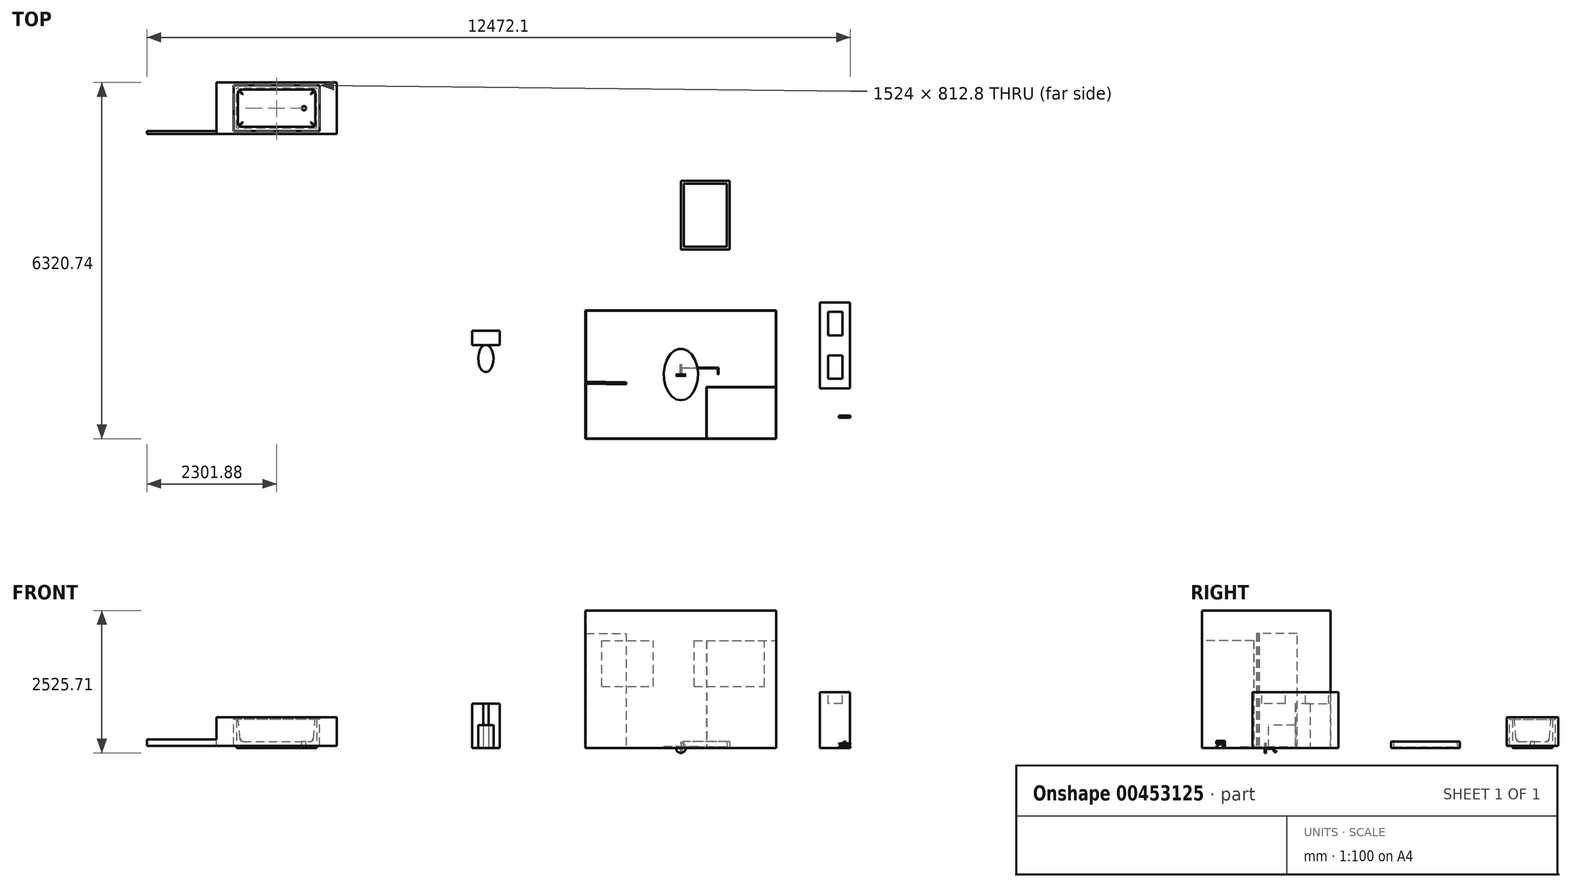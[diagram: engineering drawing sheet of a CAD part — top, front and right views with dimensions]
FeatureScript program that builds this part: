
annotation { "Feature Type Name" : "Feature", "Feature Type Description" : "" }
export const myFeature = defineFeature(function(context is Context, id is Id, definition is map)
    precondition{}
    {
        {
            var Q0;
            Q0=qCreatedBy(makeId("Top.planeOp"),FACE);
            var sketch = newSketch(context, id + "F0", { "sketchPlane" : qUnion([Q0])});
            skLineSegment(sketch, "E0.bottom", {"start": v(1684.34, 1131.89) * mm, "end": v(-1684.34, 1131.89) * mm});
            skLineSegment(sketch, "E0.top", {"start": v(1684.34, -1131.89) * mm, "end": v(-1684.34, -1131.89) * mm});
            skLineSegment(sketch, "E0.left", {"start": v(1684.34, 1131.89) * mm, "end": v(1684.34, -1131.89) * mm});
            skLineSegment(sketch, "E0.right", {"start": v(-1684.34, 1131.89) * mm, "end": v(-1684.34, -1131.89) * mm});
            skLineSegment(sketch, "E1.0", {"start": v(1690.69, 1138.24) * mm, "end": v(-1690.69, 1138.24) * mm});
            skLineSegment(sketch, "E1.1", {"start": v(1690.69, 1138.24) * mm, "end": v(1690.69, -1138.24) * mm});
            skLineSegment(sketch, "E1.2", {"start": v(1690.69, -1138.24) * mm, "end": v(-1690.69, -1138.24) * mm});
            skLineSegment(sketch, "E1.3", {"start": v(-1690.69, 1138.24) * mm, "end": v(-1690.69, -1138.24) * mm});
            skSolve(sketch);
        }
        {
            var Q0;
            Q0=makeQuery(id+"F0.imprint","IMPRINT",FACE,{"disambiguationData":[TD([[makeQuery(id+"F0.imprint","IMPRINT",EDGE,{"derivedFrom":sQuery(id+"F0.wireOp",EDGE,"E0.bottom")}),-1.0]])]});
            var Q1;
            {var subQ1=sQuery(id+"F0.wireOp",EDGE,"WMKTGaaz-quiy-9job-mGH0-Ok6Mli3DVS2J");Q1=makeQuery(id+"F0.imprint","IMPRINT",FACE,{"disambiguationData":[TD([[makeQuery(id+"F0.imprint","IMPRINT",EDGE,{"derivedFrom":subQ1}),-1.0]])]});}
            var Q2;
            Q2=sQuery(id+"F0.wireOp",EDGE,"E0.bottom");
            var Q3;
            Q3=sQuery(id+"F0.wireOp",EDGE,"E0.left");
            var Q4;
            Q4=sQuery(id+"F0.wireOp",EDGE,"E0.top");
            var Q5;
            Q5=sQuery(id+"F0.wireOp",EDGE,"E0.right");
            extrude(context, id + "F1", {"entities" : qUnion([Q0, Q1]), "surfaceEntities" : qUnion([Q2, Q3, Q4, Q5]), "depth" : 2438.4 * mm});
        }
        {
            var Q0;
            Q0=qCreatedBy(makeId("Top.planeOp"),FACE);
            var sketch = newSketch(context, id + "F2", { "sketchPlane" : qUnion([Q0])});
            skLineSegment(sketch, "E2.bottom", {"start": v(-6403.12, 4318.9) * mm, "end": v(-7927.12, 4318.9) * mm});
            skLineSegment(sketch, "E2.top", {"start": v(-6403.12, 5131.7) * mm, "end": v(-7927.12, 5131.7) * mm});
            skLineSegment(sketch, "E2.left", {"start": v(-6403.12, 4318.9) * mm, "end": v(-6403.12, 5131.7) * mm});
            skLineSegment(sketch, "E2.right", {"start": v(-7927.12, 4318.9) * mm, "end": v(-7927.12, 5131.7) * mm});
            skPoint(sketch, "E2.middle", {"position": v(-7165.12, 4725.3) * mm});
            skSolve(sketch);
        }
        {
            var Q0;
            Q0 = qSketchRegion(id + "F2", true);
            extrude(context, id + "F3", {"entities" : qUnion([Q0]), "depth" : 546.1 * mm});
        }
        {
            var Q0;
            Q0=makeQuery(id+"F3.opExtrude","CAP_FACE",FACE,{"disambiguationData":[OSD([sQuery(id+"F2.wireOp",EDGE,"E2.bottom"),sQuery(id+"F2.wireOp",EDGE,"E2.top"),sQuery(id+"F2.wireOp",EDGE,"E2.left"),sQuery(id+"F2.wireOp",EDGE,"E2.right")])],"isStart":false});
            var sketch = newSketch(context, id + "F4", { "sketchPlane" : qUnion([Q0])});
            skLineSegment(sketch, "E3.bottom", {"start": v(-6530.12, 5055.5) * mm, "end": v(-7800.12, 5055.5) * mm});
            skLineSegment(sketch, "E3.top", {"start": v(-6530.12, 4395.1) * mm, "end": v(-7800.12, 4395.1) * mm});
            skLineSegment(sketch, "E3.left", {"start": v(-6479.32, 5004.7) * mm, "end": v(-6479.32, 4445.9) * mm});
            skLineSegment(sketch, "E3.right", {"start": v(-7850.92, 5004.7) * mm, "end": v(-7850.92, 4445.9) * mm});
            skPoint(sketch, "E3.middle", {"position": v(-7165.12, 4725.3) * mm});
            skPoint(sketch, "E4.visualSharp", {"position": v(-7850.92, 5055.5) * mm});
            skArc(sketch, "E4.filletArc", {"start": v(-7800.12, 5055.5) * mm, "mid": v(-7836.05, 5040.62) * mm, "end": v(-7850.92, 5004.7) * mm});
            skPoint(sketch, "E5.visualSharp", {"position": v(-7850.92, 4395.1) * mm});
            skArc(sketch, "E5.filletArc", {"start": v(-7850.92, 4445.9) * mm, "mid": v(-7836.05, 4409.98) * mm, "end": v(-7800.12, 4395.1) * mm});
            skPoint(sketch, "E6.visualSharp", {"position": v(-6479.32, 4395.1) * mm});
            skArc(sketch, "E6.filletArc", {"start": v(-6530.12, 4395.1) * mm, "mid": v(-6494.2, 4409.98) * mm, "end": v(-6479.32, 4445.9) * mm});
            skPoint(sketch, "E7.visualSharp", {"position": v(-6479.32, 5055.5) * mm});
            skArc(sketch, "E7.filletArc", {"start": v(-6479.32, 5004.7) * mm, "mid": v(-6494.2, 5040.62) * mm, "end": v(-6530.12, 5055.5) * mm});
            skSolve(sketch);
        }
        {
            var Q0;
            Q0=makeQuery(id+"F4.imprint","IMPRINT",FACE,{"disambiguationData":[TD([[makeQuery(id+"F4.imprint","IMPRINT",EDGE,{"derivedFrom":sQuery(id+"F4.wireOp",EDGE,"E3.bottom")}),1.0]])]});
            extrude(context, id + "F5", {"entities" : qUnion([Q0]), "operationType" : NewBodyOperationType.REMOVE, "oppositeDirection" : true, "depth" : 431.8 * mm, "hasDraft" : true, "draftAngle" : 5 * degree, "draftPullDirection" : true});
        }
        {
            var Q0;
            Q0=makeQuery(id+"F3.opExtrude","CAP_FACE",FACE,{"disambiguationData":[OSD([sQuery(id+"F2.wireOp",EDGE,"E2.bottom"),sQuery(id+"F2.wireOp",EDGE,"E2.top"),sQuery(id+"F2.wireOp",EDGE,"E2.left"),sQuery(id+"F2.wireOp",EDGE,"E2.right")])],"isStart":false});
            var sketch = newSketch(context, id + "F6", { "sketchPlane" : qUnion([Q0])});
            skLineSegment(sketch, "E8.0.0", {"start": v(-6403.12, 4318.9) * mm, "end": v(-6403.12, 5131.7) * mm});
            skLineSegment(sketch, "E8.0.1", {"start": v(-6403.12, 5131.7) * mm, "end": v(-7927.12, 5131.7) * mm});
            skLineSegment(sketch, "E8.0.2", {"start": v(-7927.12, 5131.7) * mm, "end": v(-7927.12, 4318.9) * mm});
            skLineSegment(sketch, "E8.0.3", {"start": v(-7927.12, 4318.9) * mm, "end": v(-6403.12, 4318.9) * mm});
            skLineSegment(sketch, "E9.0", {"start": v(-6352.32, 5182.5) * mm, "end": v(-7977.92, 5182.5) * mm});
            skLineSegment(sketch, "E9.1", {"start": v(-6352.32, 4268.1) * mm, "end": v(-6352.32, 5182.5) * mm});
            skLineSegment(sketch, "E9.2", {"start": v(-7977.92, 4268.1) * mm, "end": v(-6352.32, 4268.1) * mm});
            skLineSegment(sketch, "E9.3", {"start": v(-7977.92, 5182.5) * mm, "end": v(-7977.92, 4268.1) * mm});
            skSolve(sketch);
        }
        {
            var Q0;
            Q0 = qSketchRegion(id + "F6", true);
            var Q1;
            Q1=makeQuery(id+"F3.opExtrude","CAP_FACE",FACE,{"disambiguationData":[OSD([sQuery(id+"F2.wireOp",EDGE,"E2.bottom"),sQuery(id+"F2.wireOp",EDGE,"E2.top"),sQuery(id+"F2.wireOp",EDGE,"E2.left"),sQuery(id+"F2.wireOp",EDGE,"E2.right")])],"isStart":true});
            extrude(context, id + "F7", {"entities" : qUnion([Q0]), "oppositeDirection" : true, "endBoundEntityFace" : qUnion([Q1]), "depth" : 508 * mm});
        }
        {
            var Q0;
            Q0=makeQuery(id+"F1.opExtrude","SWEPT_FACE",FACE,{"disambiguationData":[OSD([sQuery(id+"F0.wireOp",EDGE,"E0.bottom")])]});
            var sketch = newSketch(context, id + "F8", { "sketchPlane" : qUnion([Q0])});
            skLineSegment(sketch, "E10.bottom", {"start": v(-1404.94, 1092.2) * mm, "end": v(-490.54, 1092.2) * mm});
            skLineSegment(sketch, "E10.top", {"start": v(-1404.94, 1905) * mm, "end": v(-490.54, 1905) * mm});
            skLineSegment(sketch, "E10.left", {"start": v(-1404.94, 1092.2) * mm, "end": v(-1404.94, 1905) * mm});
            skLineSegment(sketch, "E10.right", {"start": v(-490.54, 1092.2) * mm, "end": v(-490.54, 1905) * mm});
            skLineSegment(sketch, "E11.bottom", {"start": v(233.36, 1092.2) * mm, "end": v(1481.14, 1092.2) * mm});
            skLineSegment(sketch, "E11.top", {"start": v(233.36, 1905) * mm, "end": v(1481.14, 1905) * mm});
            skLineSegment(sketch, "E11.left", {"start": v(233.36, 1092.2) * mm, "end": v(233.36, 1905) * mm});
            skLineSegment(sketch, "E11.right", {"start": v(1481.14, 1092.2) * mm, "end": v(1481.14, 1905) * mm});
            skSolve(sketch);
        }
        {
            var Q0;
            Q0 = qSketchRegion(id + "F8", true);
            extrude(context, id + "F9", {"entities" : qUnion([Q0]), "operationType" : NewBodyOperationType.REMOVE, "endBound" : BoundingType.THROUGH_ALL, "oppositeDirection" : true, "depth" : 25.4 * mm});
        }
        {
            var Q0;
            Q0=qCreatedBy(makeId("Top.planeOp"),FACE);
            var sketch = newSketch(context, id + "F10", { "sketchPlane" : qUnion([Q0])});
            skEllipse(sketch, "E12", {"center": v(-3457.47, 284.68) * mm, "majorRadius": 240.93 * mm, "minorRadius": 135.6 * mm, "majorAxis": v(0, 1)});
            skLineSegment(sketch, "E13.bottom", {"start": v(-3701.15, 777.17) * mm, "end": v(-3213.79, 777.17) * mm});
            skLineSegment(sketch, "E13.top", {"start": v(-3701.15, 525.6) * mm, "end": v(-3213.79, 525.6) * mm});
            skLineSegment(sketch, "E13.left", {"start": v(-3701.15, 777.17) * mm, "end": v(-3701.15, 525.6) * mm});
            skLineSegment(sketch, "E13.right", {"start": v(-3213.79, 777.17) * mm, "end": v(-3213.79, 525.6) * mm});
            skPoint(sketch, "E14", {"position": v(-3457.47, 43.75) * mm});
            skPoint(sketch, "E15", {"position": v(-3457.47, 525.6) * mm});
            skLineSegment(sketch, "E16.bottom", {"start": v(-3410.99, 490.28) * mm, "end": v(-3503.95, 490.28) * mm});
            skLineSegment(sketch, "E16.top", {"start": v(-3410.99, 560.94) * mm, "end": v(-3503.95, 560.94) * mm});
            skLineSegment(sketch, "E16.left", {"start": v(-3410.99, 490.28) * mm, "end": v(-3410.99, 560.94) * mm});
            skLineSegment(sketch, "E16.right", {"start": v(-3503.95, 490.28) * mm, "end": v(-3503.95, 560.94) * mm});
            skSolve(sketch);
        }
        {
            var Q0;
            Q0 = qSketchRegion(id + "F10", true);
            extrude(context, id + "F11", {"entities" : qUnion([Q0]), "depth" : 784.22 * mm});
        }
        {
            var Q0;
            Q0=makeQuery(id+"F11.opExtrude","CAP_FACE",FACE,{"disambiguationData":[OSD([sQuery(id+"F10.wireOp",EDGE,"E12"),sQuery(id+"F10.wireOp",EDGE,"E13.bottom"),sQuery(id+"F10.wireOp",EDGE,"E13.top"),sQuery(id+"F10.wireOp",EDGE,"E13.left"),sQuery(id+"F10.wireOp",EDGE,"E13.right"),sQuery(id+"F10.wireOp",EDGE,"E16.left"),sQuery(id+"F10.wireOp",EDGE,"E16.right")])],"isStart":false});
            var sketch = newSketch(context, id + "F12", { "sketchPlane" : qUnion([Q0])});
            skEllipse(sketch, "E17", {"center": v(-3457.47, 284.68) * mm, "majorRadius": 240.93 * mm, "minorRadius": 135.6 * mm, "majorAxis": v(0, -1)});
            skSolve(sketch);
        }
        {
            var Q0;
            Q0 = qSketchRegion(id + "F12", true);
            extrude(context, id + "F13", {"entities" : qUnion([Q0]), "operationType" : NewBodyOperationType.REMOVE, "oppositeDirection" : true, "depth" : 381 * mm});
        }
        {
            var Q0;
            Q0=qCreatedBy(makeId("Top.planeOp"),FACE);
            var sketch = newSketch(context, id + "F14", { "sketchPlane" : qUnion([Q0])});
            skLineSegment(sketch, "E18.bottom", {"start": v(2998.1, 1279.9) * mm, "end": v(2464.7, 1279.9) * mm});
            skLineSegment(sketch, "E18.top", {"start": v(2998.1, -244.1) * mm, "end": v(2464.7, -244.1) * mm});
            skLineSegment(sketch, "E18.left", {"start": v(2998.1, 1279.9) * mm, "end": v(2998.1, -244.1) * mm});
            skLineSegment(sketch, "E18.right", {"start": v(2464.7, 1279.9) * mm, "end": v(2464.7, -244.1) * mm});
            skSolve(sketch);
        }
        {
            var Q0;
            Q0 = qSketchRegion(id + "F14", true);
            extrude(context, id + "F15", {"entities" : qUnion([Q0]), "depth" : 988.06 * mm});
        }
        {
            var Q0;
            Q0=makeQuery(id+"F15.opExtrude","CAP_FACE",FACE,{"disambiguationData":[OSD([sQuery(id+"F14.wireOp",EDGE,"E18.bottom"),sQuery(id+"F14.wireOp",EDGE,"E18.top"),sQuery(id+"F14.wireOp",EDGE,"E18.left"),sQuery(id+"F14.wireOp",EDGE,"E18.right")])],"isStart":false});
            var sketch = newSketch(context, id + "F16", { "sketchPlane" : qUnion([Q0])});
            skLineSegment(sketch, "E19.bottom", {"start": v(2864.43, 340.03) * mm, "end": v(2613.3, 340.03) * mm});
            skLineSegment(sketch, "E19.top", {"start": v(2864.43, -75.86) * mm, "end": v(2613.3, -75.86) * mm});
            skLineSegment(sketch, "E19.left", {"start": v(2864.43, 340.03) * mm, "end": v(2864.43, -75.86) * mm});
            skLineSegment(sketch, "E19.right", {"start": v(2613.3, 340.03) * mm, "end": v(2613.3, -75.86) * mm});
            skLineSegment(sketch, "E20", {"start": v(2464.7, 517.9) * mm, "end": v(2998.1, 517.9) * mm, "construction": true});
            skLineSegment(sketch, "E21.MirrorCS", {"start": v(2864.43, 695.77) * mm, "end": v(2613.3, 695.77) * mm});
            skLineSegment(sketch, "E22.MirrorCS", {"start": v(2864.43, 695.77) * mm, "end": v(2864.43, 1111.67) * mm});
            skLineSegment(sketch, "E23.MirrorCS", {"start": v(2864.43, 1111.67) * mm, "end": v(2613.3, 1111.67) * mm});
            skLineSegment(sketch, "E24.MirrorCS", {"start": v(2613.3, 695.77) * mm, "end": v(2613.3, 1111.67) * mm});
            skSolve(sketch);
        }
        {
            var Q0;
            Q0 = qSketchRegion(id + "F16", true);
            extrude(context, id + "F17", {"entities" : qUnion([Q0]), "operationType" : NewBodyOperationType.REMOVE, "oppositeDirection" : true, "depth" : 203.2 * mm});
        }
        {
            var Q0;
            Q0=makeQuery(id+"F1.opExtrude","SWEPT_FACE",FACE,{"disambiguationData":[OSD([sQuery(id+"F0.wireOp",EDGE,"E1.3")])]});
            var sketch = newSketch(context, id + "F18", { "sketchPlane" : qUnion([Q0])});
            skLineSegment(sketch, "E25.bottom", {"start": v(-547.69, 0) * mm, "end": v(163.51, 0) * mm});
            skLineSegment(sketch, "E25.top", {"start": v(-547.69, 2032) * mm, "end": v(163.51, 2032) * mm});
            skLineSegment(sketch, "E25.left", {"start": v(-547.69, 0) * mm, "end": v(-547.69, 2032) * mm});
            skLineSegment(sketch, "E25.right", {"start": v(163.51, 0) * mm, "end": v(163.51, 2032) * mm});
            skSolve(sketch);
        }
        {
            var Q0;
            Q0 = qSketchRegion(id + "F18", true);
            extrude(context, id + "F19", {"entities" : qUnion([Q0]), "operationType" : NewBodyOperationType.REMOVE, "endBound" : BoundingType.UP_TO_NEXT, "oppositeDirection" : true, "depth" : 25.4 * mm});
        }
        {
            var Q0;
            Q0=qCreatedBy(makeId("Top.planeOp"),FACE);
            var sketch = newSketch(context, id + "F20", { "sketchPlane" : qUnion([Q0])});
            skLineSegment(sketch, "E26.bottom", {"start": v(3005.06, -730.01) * mm, "end": v(2801.86, -730.01) * mm});
            skLineSegment(sketch, "E26.top", {"start": v(3005.06, -768.11) * mm, "end": v(2801.86, -768.11) * mm});
            skLineSegment(sketch, "E26.left", {"start": v(3005.06, -730.01) * mm, "end": v(3005.06, -768.11) * mm});
            skLineSegment(sketch, "E26.right", {"start": v(2801.86, -730.01) * mm, "end": v(2801.86, -768.11) * mm});
            skLineSegment(sketch, "E27.bottom", {"start": v(2916.16, -768.11) * mm, "end": v(2890.76, -768.11) * mm});
            skLineSegment(sketch, "E27.top", {"start": v(2916.16, -882.41) * mm, "end": v(2890.76, -882.41) * mm});
            skLineSegment(sketch, "E27.left", {"start": v(2890.76, -768.11) * mm, "end": v(2890.76, -882.41) * mm});
            skLineSegment(sketch, "E27.right", {"start": v(2916.16, -768.11) * mm, "end": v(2916.16, -882.41) * mm});
            skLineSegment(sketch, "E28", {"start": v(2903.46, -882.41) * mm, "end": v(2903.46, -768.11) * mm, "construction": true});
            skSolve(sketch);
        }
        {
            var Q0;
            Q0=makeQuery(id+"F20.imprint","IMPRINT",FACE,{"disambiguationData":[TD([[makeQuery(id+"F20.imprint","IMPRINT",EDGE,{"derivedFrom":sQuery(id+"F20.wireOp",EDGE,"E26.bottom")}),1.0]])]});
            var Q1;
            Q1=makeQuery(id+"F20.imprint","IMPRINT",FACE,{"disambiguationData":[TD([[makeQuery(id+"F20.imprint","IMPRINT",EDGE,{"derivedFrom":sQuery(id+"F20.wireOp",EDGE,"E27.bottom")}),1.0]])]});
            extrude(context, id + "F21", {"entities" : qUnion([Q0, Q1]), "depth" : 127 * mm});
        }
        {
            var Q0;
            Q0=makeQuery(id+"F21.opExtrude","SWEPT_FACE",FACE,{"disambiguationData":[OSD([sQuery(id+"F20.wireOp",EDGE,"E26.left")])]});
            var sketch = newSketch(context, id + "F22", { "sketchPlane" : qUnion([Q0])});
            skFitSpline(sketch, "E29", {"points": [v(-730.01, 115.54) * mm, v(-807.64, 106.92) * mm, v(-882.41, 66.8) * mm], "startDerivative": vector(-174.08, -1.43) * mm, "endDerivative": vector(-147.56, -98.42) * mm});
            skFitSpline(sketch, "E30", {"points": [v(-730.01, 72.48) * mm, v(-792.44, 72.94) * mm, v(-882.41, 39.52) * mm], "startDerivative": vector(-134.64, 14.8) * mm, "endDerivative": vector(-167.34, -77.47) * mm});
            skLineSegment(sketch, "E31.bottom", {"start": v(-882.41, 66.8) * mm, "end": v(-852.3, 66.8) * mm});
            skLineSegment(sketch, "E31.top", {"start": v(-882.41, 38.63) * mm, "end": v(-852.3, 38.63) * mm});
            skLineSegment(sketch, "E31.left", {"start": v(-882.41, 66.8) * mm, "end": v(-882.41, 38.63) * mm});
            skLineSegment(sketch, "E31.right", {"start": v(-852.3, 66.8) * mm, "end": v(-852.3, 38.63) * mm});
            skLineSegment(sketch, "E32.bottom", {"start": v(-882.41, 38.63) * mm, "end": v(-882.41, 38.63) * mm});
            skLineSegment(sketch, "E32.top", {"start": v(-882.41, 39.52) * mm, "end": v(-882.41, 39.52) * mm});
            skLineSegment(sketch, "E32.left", {"start": v(-882.41, 38.63) * mm, "end": v(-882.41, 39.52) * mm});
            skLineSegment(sketch, "E32.right", {"start": v(-882.41, 38.63) * mm, "end": v(-882.41, 39.52) * mm});
            skLineSegment(sketch, "E33.0.0", {"start": v(-768.11, 0) * mm, "end": v(-730.01, 0) * mm});
            skLineSegment(sketch, "E33.0.1", {"start": v(-730.01, 0) * mm, "end": v(-730.01, 127) * mm});
            skLineSegment(sketch, "E33.0.2", {"start": v(-730.01, 127) * mm, "end": v(-768.11, 127) * mm});
            skLineSegment(sketch, "E33.0.3", {"start": v(-768.11, 127) * mm, "end": v(-768.11, 0) * mm});
            skLineSegment(sketch, "E34.0.0", {"start": v(-882.41, 0) * mm, "end": v(-768.11, 0) * mm});
            skLineSegment(sketch, "E34.0.1", {"start": v(-768.11, 0) * mm, "end": v(-768.11, 127) * mm});
            skLineSegment(sketch, "E34.0.2", {"start": v(-768.11, 127) * mm, "end": v(-882.41, 127) * mm});
            skLineSegment(sketch, "E34.0.3", {"start": v(-882.41, 127) * mm, "end": v(-882.41, 0) * mm});
            skSolve(sketch);
        }
        {
            var Q0;
            {var subQ5=sQuery(id+"F22.wireOp",EDGE,"E33.0.2");Q0=makeQuery(id+"F22.imprint","IMPRINT",FACE,{"disambiguationData":[TD([[makeQuery(id+"F22.imprint","IMPRINT",EDGE,{"derivedFrom":subQ5}),1.0]])]});}
            var Q1;
            {var subQ5=sQuery(id+"F22.wireOp",EDGE,"E34.0.2");Q1=makeQuery(id+"F22.imprint","IMPRINT",FACE,{"disambiguationData":[TD([[makeQuery(id+"F22.imprint","IMPRINT",EDGE,{"derivedFrom":subQ5}),1.0]])]});}
            var Q2;
            {var subQ6=sQuery(id+"F22.wireOp",EDGE,"E31.top");Q2=makeQuery(id+"F22.imprint","IMPRINT",FACE,{"disambiguationData":[TD([[makeQuery(id+"F22.imprint","IMPRINT",EDGE,{"derivedFrom":subQ6}),-1.0]])]});}
            extrude(context, id + "F23", {"entities" : qUnion([Q0, Q1, Q2]), "operationType" : NewBodyOperationType.REMOVE, "endBound" : BoundingType.THROUGH_ALL, "oppositeDirection" : true, "depth" : 25.4 * mm});
        }
        {
            var Q0;
            Q0=makeQuery(id+"F21.opExtrude","SWEPT_FACE",FACE,{"disambiguationData":[OSD([sQuery(id+"F20.wireOp",EDGE,"E26.bottom")])]});
            var sketch = newSketch(context, id + "F24", { "sketchPlane" : qUnion([Q0])});
            skLineSegment(sketch, "E35.0.0", {"start": v(-2801.86, 0) * mm, "end": v(-2801.86, 115.54) * mm});
            skLineSegment(sketch, "E35.0.1", {"start": v(-2801.86, 115.54) * mm, "end": v(-3005.06, 115.54) * mm});
            skLineSegment(sketch, "E35.0.2", {"start": v(-3005.06, 115.54) * mm, "end": v(-3005.06, 0) * mm});
            skLineSegment(sketch, "E35.0.3", {"start": v(-3005.06, 0) * mm, "end": v(-2801.86, 0) * mm});
            skLineSegment(sketch, "E36.top", {"start": v(-3005.06, 25.4) * mm, "end": v(-2801.86, 25.4) * mm});
            skLineSegment(sketch, "E36.left", {"start": v(-3005.06, 0) * mm, "end": v(-3005.06, 25.4) * mm});
            skLineSegment(sketch, "E36.right", {"start": v(-2801.86, 0) * mm, "end": v(-2801.86, 25.4) * mm});
            skLineSegment(sketch, "E37", {"start": v(-2966.35, 25.4) * mm, "end": v(-2966.35, 68.22) * mm});
            skLineSegment(sketch, "E38", {"start": v(-2966.35, 68.22) * mm, "end": v(-3005.06, 68.22) * mm});
            skLineSegment(sketch, "E39", {"start": v(-3005.06, 68.22) * mm, "end": v(-3005.06, 78.75) * mm});
            skLineSegment(sketch, "E40", {"start": v(-3005.06, 78.75) * mm, "end": v(-2935.24, 78.75) * mm});
            skLineSegment(sketch, "E41", {"start": v(-2935.24, 78.75) * mm, "end": v(-2935.24, 25.4) * mm});
            skLineSegment(sketch, "E42", {"start": v(-2903.46, 115.54) * mm, "end": v(-2903.46, 149.96) * mm, "construction": true});
            skPoint(sketch, "E42.endSnap0", {"position": v(-2903.46, 115.54) * mm});
            skLineSegment(sketch, "E43.MirrorCS", {"start": v(-2871.68, 78.75) * mm, "end": v(-2871.68, 25.4) * mm});
            skLineSegment(sketch, "E44.MirrorCS", {"start": v(-2801.86, 78.75) * mm, "end": v(-2871.68, 78.75) * mm});
            skLineSegment(sketch, "E45.MirrorCS", {"start": v(-2801.86, 68.22) * mm, "end": v(-2801.86, 78.75) * mm});
            skLineSegment(sketch, "E46.MirrorCS", {"start": v(-2840.57, 68.22) * mm, "end": v(-2801.86, 68.22) * mm});
            skLineSegment(sketch, "E47.MirrorCS", {"start": v(-2840.57, 25.4) * mm, "end": v(-2840.57, 68.22) * mm});
            skLineSegment(sketch, "E48", {"start": v(-2916.16, 115.54) * mm, "end": v(-2916.16, 25.4) * mm});
            skLineSegment(sketch, "E49", {"start": v(-2890.76, 115.54) * mm, "end": v(-2890.76, 25.4) * mm});
            skPoint(sketch, "E49.endSnap0", {"position": v(-2903.46, 25.4) * mm});
            skSolve(sketch);
        }
        {
            var Q0;
            {var subQ4=sQuery(id+"F24.wireOp",EDGE,"E37");Q0=makeQuery(id+"F24.imprint","IMPRINT",FACE,{"disambiguationData":[TD([[makeQuery(id+"F24.imprint","IMPRINT",EDGE,{"derivedFrom":subQ4}),1.0]])]});}
            var Q1;
            {var subQ0=sQuery(id+"F24.wireOp",EDGE,"E40");Q1=makeQuery(id+"F24.imprint","IMPRINT",FACE,{"disambiguationData":[TD([[makeQuery(id+"F24.imprint","IMPRINT",EDGE,{"derivedFrom":subQ0}),1.0]])]});}
            var Q2;
            {var subQ0=sQuery(id+"F24.wireOp",EDGE,"E43.MirrorCS");Q2=makeQuery(id+"F24.imprint","IMPRINT",FACE,{"disambiguationData":[TD([[makeQuery(id+"F24.imprint","IMPRINT",EDGE,{"derivedFrom":subQ0}),-1.0]])]});}
            var Q3;
            {var subQ3=sQuery(id+"F24.wireOp",EDGE,"E46.MirrorCS");Q3=makeQuery(id+"F24.imprint","IMPRINT",FACE,{"disambiguationData":[TD([[makeQuery(id+"F24.imprint","IMPRINT",EDGE,{"derivedFrom":subQ3}),-1.0]])]});}
            extrude(context, id + "F25", {"entities" : qUnion([Q0, Q1, Q2, Q3]), "operationType" : NewBodyOperationType.REMOVE, "endBound" : BoundingType.THROUGH_ALL, "oppositeDirection" : true, "depth" : 25.4 * mm});
        }
        {
            var Q0;
            Q0=makeQuery(id+"F25.boolean.opBoolean","COPY",EDGE,{"derivedFrom":makeQuery(id+"F25.opExtrude","SWEPT_EDGE",EDGE,{"disambiguationData":[OSD([sQuery(id+"F24.wireOp",EDGE,"E36.top"),sQuery(id+"F24.wireOp",EDGE,"E37")])]})});
            var Q1;
            Q1=makeQuery(id+"F25.boolean.opBoolean","COPY",EDGE,{"derivedFrom":makeQuery(id+"F25.opExtrude","SWEPT_EDGE",EDGE,{"disambiguationData":[OSD([sQuery(id+"F24.wireOp",EDGE,"E36.top"),sQuery(id+"F24.wireOp",EDGE,"E48")])]})});
            var Q2;
            Q2=makeQuery(id+"F25.boolean.opBoolean","COPY",EDGE,{"derivedFrom":makeQuery(id+"F25.opExtrude","SWEPT_EDGE",EDGE,{"disambiguationData":[OSD([sQuery(id+"F24.wireOp",EDGE,"E36.top"),sQuery(id+"F24.wireOp",EDGE,"E41")])]})});
            var Q3;
            Q3=makeQuery(id+"F25.boolean.opBoolean","COPY",EDGE,{"derivedFrom":makeQuery(id+"F25.opExtrude","SWEPT_EDGE",EDGE,{"disambiguationData":[OSD([sQuery(id+"F24.wireOp",EDGE,"E36.top"),sQuery(id+"F24.wireOp",EDGE,"E49")])]})});
            var Q4;
            Q4=makeQuery(id+"F25.boolean.opBoolean","COPY",EDGE,{"derivedFrom":makeQuery(id+"F25.opExtrude","SWEPT_EDGE",EDGE,{"disambiguationData":[OSD([sQuery(id+"F24.wireOp",EDGE,"E36.top"),sQuery(id+"F24.wireOp",EDGE,"E43.MirrorCS")])]})});
            var Q5;
            Q5=makeQuery(id+"F25.boolean.opBoolean","COPY",EDGE,{"derivedFrom":makeQuery(id+"F25.opExtrude","SWEPT_EDGE",EDGE,{"disambiguationData":[OSD([sQuery(id+"F24.wireOp",EDGE,"E36.top"),sQuery(id+"F24.wireOp",EDGE,"E47.MirrorCS")])]})});
            var Q6;
            Q6=makeQuery(id+"F23.boolean.opBoolean","COPY",EDGE,{"derivedFrom":makeQuery(id+"F23.opExtrude","SWEPT_EDGE",EDGE,{"disambiguationData":[OSD([sQuery(id+"F22.wireOp",EDGE,"E29"),sQuery(id+"F22.wireOp",EDGE,"E33.0.1")])]})});
            var Q7;
            Q7=makeQuery(id+"F23.boolean.opBoolean","COPY",EDGE,{"derivedFrom":makeQuery(id+"F23.opExtrude","SWEPT_EDGE",EDGE,{"disambiguationData":[OSD([sQuery(id+"F22.wireOp",EDGE,"E30"),sQuery(id+"F22.wireOp",EDGE,"E34.0.1")])]})});
            fillet(context, id + "F26", {"entities" : qUnion([Q0, Q1, Q2, Q3, Q4, Q5, Q6, Q7]), "radius" : 5.08 * mm, "tangentPropagation" : true, "allowEdgeOverflow" : false});
        }
        {
            var Q0;
            Q0=qCreatedBy(makeId("Front.planeOp"),FACE);
            var sketch = newSketch(context, id + "F27", { "sketchPlane" : qUnion([Q0])});
            skCircle(sketch, "E50", {"center": v(0, 0) * mm, "radius": 87.31 * mm});
            skSolve(sketch);
        }
        {
            var Q0;
            Q0 = qSketchRegion(id + "F27", true);
            extrude(context, id + "F28", {"entities" : qUnion([Q0]), "depth" : 25.4 * mm});
        }
        {
            var Q0;
            Q0=qCreatedBy(makeId("Right.planeOp"),FACE);
            var sketch = newSketch(context, id + "F29", { "sketchPlane" : qUnion([Q0])});
            skLineSegment(sketch, "E51", {"start": v(0, 0) * mm, "end": v(96.34, 0) * mm});
            skLineSegment(sketch, "E52", {"start": v(105.32, -3.72) * mm, "end": v(173.44, -71.84) * mm});
            skPoint(sketch, "E53.visualSharp", {"position": v(101.6, 0) * mm});
            skArc(sketch, "E53.filletArc", {"start": v(105.32, -3.72) * mm, "mid": v(101.2, -0.97) * mm, "end": v(96.34, 0) * mm});
            skSolve(sketch);
        }
        {
            var Q0;
            Q0=makeQuery(id+"F28.opExtrude","CAP_FACE",FACE,{"disambiguationData":[OSD([sQuery(id+"F27.wireOp",EDGE,"E50")])],"isStart":true});
            var sketch = newSketch(context, id + "F30", { "sketchPlane" : qUnion([Q0])});
            skCircle(sketch, "E54", {"center": v(0, 0) * mm, "radius": 12.7 * mm});
            skSolve(sketch);
        }
        {
            var Q0;
            Q0=makeQuery(id+"F30.imprint","IMPRINT",FACE,{"disambiguationData":[TD([[makeQuery(id+"F30.imprint","IMPRINT",EDGE,{"derivedFrom":sQuery(id+"F30.wireOp",EDGE,"E54")}),1.0]])]});
            var Q1;
            Q1=sQuery(id+"F29.wireOp",EDGE,"E51");
            var Q2;
            Q2=sQuery(id+"F29.wireOp",EDGE,"E52");
            var Q3;
            Q3=sQuery(id+"F29.wireOp",EDGE,"E53.filletArc");
            sweep(context, id + "F31", {"operationType" : NewBodyOperationType.ADD, "profiles" : qUnion([Q0]), "path" : qUnion([Q1, Q2, Q3])});
        }
        {
            var Q0;
            Q0=qCreatedBy(makeId("Top.planeOp"),FACE);
            var sketch = newSketch(context, id + "F32", { "sketchPlane" : qUnion([Q0])});
            skLineSegment(sketch, "E55.0", {"start": v(1684.34, 1131.89) * mm, "end": v(-1684.34, 1131.89) * mm});
            skLineSegment(sketch, "E56", {"start": v(449.26, -217.49) * mm, "end": v(449.26, -1131.89) * mm});
            skLineSegment(sketch, "E57.0", {"start": v(1684.34, 1131.89) * mm, "end": v(1684.34, -1131.89) * mm});
            skLineSegment(sketch, "E58", {"start": v(449.26, -217.49) * mm, "end": v(1684.34, -217.49) * mm});
            skLineSegment(sketch, "E59.1", {"start": v(1684.34, -1131.89) * mm, "end": v(-1684.34, -1131.89) * mm});
            skLineSegment(sketch, "E60.0", {"start": v(455.61, -223.84) * mm, "end": v(1684.34, -223.84) * mm});
            skLineSegment(sketch, "E60.1", {"start": v(455.61, -223.84) * mm, "end": v(455.61, -1131.89) * mm});
            skSolve(sketch);
        }
        {
            var Q0;
            {var subQ3=sQuery(id+"F32.wireOp",EDGE,"E56");Q0=makeQuery(id+"F32.imprint","IMPRINT",FACE,{"disambiguationData":[TD([[makeQuery(id+"F32.imprint","IMPRINT",EDGE,{"derivedFrom":subQ3}),1.0]])]});}
            var Q1;
            Q1=makeQuery(id+"F9.boolean.opBoolean","COPY",VERTEX,{"derivedFrom":makeQuery(id+"F9.opExtrude","CAP_VERTEX",VERTEX,{"disambiguationData":[OSD([sQuery(id+"F8.wireOp",EDGE,"E11.top"),sQuery(id+"F8.wireOp",EDGE,"E11.left")])],"isStart":true})});
            extrude(context, id + "F33", {"entities" : qUnion([Q0]), "operationType" : NewBodyOperationType.ADD, "endBound" : BoundingType.UP_TO_VERTEX, "endBoundEntityVertex" : qUnion([Q1]), "depth" : 25.4 * mm});
        }
        {
            var Q0;
            Q0=qCreatedBy(makeId("Top.planeOp"),FACE);
            var sketch = newSketch(context, id + "F34", { "sketchPlane" : qUnion([Q0])});
            skPoint(sketch, "E61.0", {"position": v(-1684.34, -163.51) * mm});
            skLineSegment(sketch, "E62.bottom", {"start": v(-1684.34, -163.51) * mm, "end": v(-973.25, -175.92) * mm});
            skLineSegment(sketch, "E62.top", {"start": v(-1683.67, -125.42) * mm, "end": v(-972.58, -137.83) * mm});
            skLineSegment(sketch, "E62.left", {"start": v(-1683.67, -125.42) * mm, "end": v(-1684.34, -163.51) * mm});
            skLineSegment(sketch, "E62.right", {"start": v(-972.58, -137.83) * mm, "end": v(-973.25, -175.92) * mm});
            skLineSegment(sketch, "E63", {"start": v(-1683.67, -125.42) * mm, "end": v(-1684.34, -125.42) * mm});
            skLineSegment(sketch, "E64", {"start": v(-1684.34, -125.42) * mm, "end": v(-1684.34, -163.51) * mm});
            skCircle(sketch, "E65", {"center": v(-1684.34, -163.51) * mm, "radius": 1.56 * mm});
            skSolve(sketch);
        }
        {
            var Q0;
            {var subQ2=sQuery(id+"F34.wireOp",EDGE,"E62.top");Q0=makeQuery(id+"F34.imprint","IMPRINT",FACE,{"disambiguationData":[TD([[makeQuery(id+"F34.imprint","IMPRINT",EDGE,{"derivedFrom":subQ2}),-1.0]])]});}
            var Q1;
            {var subQ1=sQuery(id+"F34.wireOp",EDGE,"E62.bottom");var subQ3=sQuery(id+"F34.wireOp",EDGE,"E65");var subQ4=makeQuery(id+"F34.imprint","INTERSECT",VERTEX,{"derivedFrom":[subQ1,subQ3]});Q1=makeQuery(id+"F34.imprint","IMPRINT",FACE,{"disambiguationData":[TD([[makeQuery(id+"F34.imprint","IMPRINT",EDGE,{"disambiguationData":[TD([[subQ4,-1.0]])],"derivedFrom":subQ3}),1.0]])]});}
            var Q2;
            {var subQ1=sQuery(id+"F34.wireOp",EDGE,"E62.bottom");var subQ3=sQuery(id+"F34.wireOp",EDGE,"E65");var subQ4=makeQuery(id+"F34.imprint","INTERSECT",VERTEX,{"derivedFrom":[subQ1,subQ3]});Q2=makeQuery(id+"F34.imprint","IMPRINT",FACE,{"disambiguationData":[TD([[makeQuery(id+"F34.imprint","IMPRINT",EDGE,{"disambiguationData":[TD([[subQ4,1.0]])],"derivedFrom":subQ3}),1.0]])]});}
            extrude(context, id + "F35", {"entities" : qUnion([Q0, Q1, Q2]), "operationType" : NewBodyOperationType.ADD, "depth" : 2032 * mm});
        }
        {
            var Q0;
            Q0=makeQuery(id+"F5.boolean.opBoolean","COPY",EDGE,{"derivedFrom":makeQuery(id+"F5.opExtrude","CAP_EDGE",EDGE,{"disambiguationData":[OSD([sQuery(id+"F4.wireOp",EDGE,"E3.bottom")])],"isStart":false})});
            fillet(context, id + "F36", {"entities" : qUnion([Q0]), "radius" : 50.8 * mm, "tangentPropagation" : true, "allowEdgeOverflow" : false});
        }
        {
            var Q0;
            Q0=makeQuery(id+"F7.opExtrude","CAP_FACE",FACE,{"disambiguationData":[OSD([sQuery(id+"F6.wireOp",EDGE,"E8.0.0"),sQuery(id+"F6.wireOp",EDGE,"E8.0.1"),sQuery(id+"F6.wireOp",EDGE,"E8.0.2"),sQuery(id+"F6.wireOp",EDGE,"E8.0.3"),sQuery(id+"F6.wireOp",EDGE,"E9.0"),sQuery(id+"F6.wireOp",EDGE,"E9.1"),sQuery(id+"F6.wireOp",EDGE,"E9.2"),sQuery(id+"F6.wireOp",EDGE,"E9.3")])],"isStart":true});
            var sketch = newSketch(context, id + "F37", { "sketchPlane" : qUnion([Q0])});
            skLineSegment(sketch, "E66.bottom", {"start": v(-7977.92, 5182.5) * mm, "end": v(-8231.92, 5182.5) * mm});
            skLineSegment(sketch, "E66.top", {"start": v(-7977.92, 4268.1) * mm, "end": v(-8231.92, 4268.1) * mm});
            skLineSegment(sketch, "E66.left", {"start": v(-7977.92, 5182.5) * mm, "end": v(-7977.92, 4268.1) * mm});
            skLineSegment(sketch, "E66.right", {"start": v(-8231.92, 5182.5) * mm, "end": v(-8231.92, 4268.1) * mm});
            skLineSegment(sketch, "E67", {"start": v(-7977.92, 4268.1) * mm, "end": v(-7977.92, 5182.5) * mm});
            skLineSegment(sketch, "E68.bottom", {"start": v(-6352.32, 5182.5) * mm, "end": v(-6098.32, 5182.5) * mm});
            skLineSegment(sketch, "E68.top", {"start": v(-6352.32, 4268.1) * mm, "end": v(-6098.32, 4268.1) * mm});
            skLineSegment(sketch, "E68.left", {"start": v(-6352.32, 5182.5) * mm, "end": v(-6352.32, 4268.1) * mm});
            skLineSegment(sketch, "E68.right", {"start": v(-6098.32, 5182.5) * mm, "end": v(-6098.32, 4268.1) * mm});
            skSolve(sketch);
        }
        {
            var Q0;
            Q0=makeQuery(id+"F37.imprint","IMPRINT",FACE,{"disambiguationData":[TD([[makeQuery(id+"F37.imprint","IMPRINT",EDGE,{"derivedFrom":sQuery(id+"F37.wireOp",EDGE,"E66.bottom")}),1.0]])]});
            var Q1;
            Q1=makeQuery(id+"F37.imprint","IMPRINT",FACE,{"disambiguationData":[TD([[makeQuery(id+"F37.imprint","IMPRINT",EDGE,{"derivedFrom":sQuery(id+"F37.wireOp",EDGE,"E68.bottom")}),-1.0]])]});
            var Q2;
            Q2=makeQuery(id+"F7.opExtrude","CAP_FACE",FACE,{"disambiguationData":[OSD([sQuery(id+"F2.wireOp",EDGE,"E2.bottom"),sQuery(id+"F2.wireOp",EDGE,"E2.top"),sQuery(id+"F2.wireOp",EDGE,"E2.left"),sQuery(id+"F2.wireOp",EDGE,"E2.right")])],"isStart":false});
            extrude(context, id + "F38", {"entities" : qUnion([Q0, Q1]), "operationType" : NewBodyOperationType.ADD, "oppositeDirection" : true, "endBoundEntityFace" : qUnion([Q2]), "depth" : 508 * mm});
        }
        {
            var Q0;
            Q0=qCreatedBy(makeId("Top.planeOp"),FACE);
            var sketch = newSketch(context, id + "F39", { "sketchPlane" : qUnion([Q0])});
            skEllipse(sketch, "E69", {"center": v(0, 0) * mm, "majorRadius": 457.2 * mm, "minorRadius": 304.8 * mm, "majorAxis": v(0, -1)});
            skSolve(sketch);
        }
        {
            var Q0;
            Q0=makeQuery(id+"F39.imprint","IMPRINT",FACE,{"disambiguationData":[TD([[makeQuery(id+"F39.imprint","IMPRINT",EDGE,{"derivedFrom":sQuery(id+"F39.wireOp",EDGE,"E69")}),1.0]])]});
            extrude(context, id + "F40", {"entities" : qUnion([Q0]), "depth" : 25.4 * mm});
        }
        {
            var Q0;
            Q0=qCreatedBy(makeId("Top.planeOp"),FACE);
            var sketch = newSketch(context, id + "F41", { "sketchPlane" : qUnion([Q0])});
            skLineSegment(sketch, "E70", {"start": v(657.35, 0) * mm, "end": v(657.35, 108.46) * mm});
            skLineSegment(sketch, "E71", {"start": v(657.35, 108.46) * mm, "end": v(12.7, 108.46) * mm});
            skLineSegment(sketch, "E72", {"start": v(12.7, 108.46) * mm, "end": v(12.7, 0) * mm});
            skLineSegment(sketch, "E73", {"start": v(12.7, 0) * mm, "end": v(0, 0) * mm});
            skLineSegment(sketch, "E74", {"start": v(0, 0) * mm, "end": v(0, 121.16) * mm});
            skLineSegment(sketch, "E75", {"start": v(0, 121.16) * mm, "end": v(670.05, 121.16) * mm});
            skLineSegment(sketch, "E76", {"start": v(670.05, 121.16) * mm, "end": v(670.05, 0) * mm});
            skLineSegment(sketch, "E77", {"start": v(670.05, 0) * mm, "end": v(657.35, 0) * mm});
            skLineSegment(sketch, "E78", {"start": v(335.03, 108.46) * mm, "end": v(335.03, 121.16) * mm});
            skPoint(sketch, "E78.endSnap0", {"position": v(335.03, 121.16) * mm});
            skSolve(sketch);
        }
        {
            var Q0;
            Q0 = qSketchRegion(id + "F41", true);
            extrude(context, id + "F42", {"entities" : qUnion([Q0]), "depth" : 12.7 * mm});
        }
        {
            var Q0;
            Q0=makeQuery(id+"F3.opExtrude","CAP_FACE",FACE,{"disambiguationData":[OSD([sQuery(id+"F2.wireOp",EDGE,"E2.bottom"),sQuery(id+"F2.wireOp",EDGE,"E2.top"),sQuery(id+"F2.wireOp",EDGE,"E2.left"),sQuery(id+"F2.wireOp",EDGE,"E2.right")])],"isStart":true});
            var sketch = newSketch(context, id + "F43", { "sketchPlane" : qUnion([Q0])});
            skLineSegment(sketch, "E79.0", {"start": v(-6453.92, -4369.7) * mm, "end": v(-7876.32, -4369.7) * mm});
            skLineSegment(sketch, "E79.1", {"start": v(-6453.92, -4369.7) * mm, "end": v(-6453.92, -5080.9) * mm});
            skLineSegment(sketch, "E79.2", {"start": v(-6453.92, -5080.9) * mm, "end": v(-7876.32, -5080.9) * mm});
            skLineSegment(sketch, "E79.3", {"start": v(-7876.32, -4369.7) * mm, "end": v(-7876.32, -5080.9) * mm});
            skLineSegment(sketch, "E80.0.0", {"start": v(-6403.12, -5131.7) * mm, "end": v(-6403.12, -4318.9) * mm});
            skLineSegment(sketch, "E80.0.1", {"start": v(-6403.12, -4318.9) * mm, "end": v(-7927.12, -4318.9) * mm});
            skLineSegment(sketch, "E80.0.2", {"start": v(-7927.12, -4318.9) * mm, "end": v(-7927.12, -5131.7) * mm});
            skLineSegment(sketch, "E80.0.3", {"start": v(-7927.12, -5131.7) * mm, "end": v(-6403.12, -5131.7) * mm});
            skSolve(sketch);
        }
        {
            var Q0;
            Q0 = qSketchRegion(id + "F43", true);
            extrude(context, id + "F44", {"entities" : qUnion([Q0]), "operationType" : NewBodyOperationType.REMOVE, "oppositeDirection" : true, "depth" : 508 * mm});
        }
        {
            var Q0;
            Q0=makeQuery(id+"F5.boolean.opBoolean","COPY",FACE,{"derivedFrom":makeQuery(id+"F5.opExtrude","CAP_FACE",FACE,{"disambiguationData":[OSD([sQuery(id+"F4.wireOp",EDGE,"E3.bottom"),sQuery(id+"F4.wireOp",EDGE,"E3.top"),sQuery(id+"F4.wireOp",EDGE,"E3.left"),sQuery(id+"F4.wireOp",EDGE,"E3.right"),sQuery(id+"F4.wireOp",EDGE,"E4.filletArc"),sQuery(id+"F4.wireOp",EDGE,"E5.filletArc"),sQuery(id+"F4.wireOp",EDGE,"E6.filletArc"),sQuery(id+"F4.wireOp",EDGE,"E7.filletArc")])],"isStart":false})});
            var sketch = newSketch(context, id + "F45", { "sketchPlane" : qUnion([Q0])});
            skLineSegment(sketch, "E81", {"start": v(-6563.65, 4725.3) * mm, "end": v(-6682.52, 4725.3) * mm, "construction": true});
            skPoint(sketch, "E81.endSnap0", {"position": v(-6563.65, 4725.3) * mm});
            skCircle(sketch, "E82", {"center": v(-6682.52, 4725.3) * mm, "radius": 38.1 * mm});
            skLineSegment(sketch, "E83.bottom", {"start": v(-6752.37, 4801.5) * mm, "end": v(-6403.12, 4801.5) * mm});
            skLineSegment(sketch, "E83.top", {"start": v(-6752.37, 4649.1) * mm, "end": v(-6403.12, 4649.1) * mm});
            skLineSegment(sketch, "E83.left", {"start": v(-6752.37, 4801.5) * mm, "end": v(-6752.37, 4649.1) * mm});
            skLineSegment(sketch, "E83.right", {"start": v(-6403.12, 4801.5) * mm, "end": v(-6403.12, 4649.1) * mm});
            skPoint(sketch, "E84.0", {"position": v(-6403.12, 4725.3) * mm});
            skSolve(sketch);
        }
        {
            var Q0;
            Q0=makeQuery(id+"F45.imprint","IMPRINT",FACE,{"disambiguationData":[TD([[makeQuery(id+"F45.imprint","IMPRINT",EDGE,{"derivedFrom":sQuery(id+"F45.wireOp",EDGE,"E82")}),1.0]])]});
            extrude(context, id + "F46", {"entities" : qUnion([Q0]), "operationType" : NewBodyOperationType.REMOVE, "endBound" : BoundingType.THROUGH_ALL, "oppositeDirection" : true, "depth" : 25.4 * mm});
        }
        {
            var Q0;
            Q0=qCreatedBy(makeId("Top.planeOp"),FACE);
            var sketch = newSketch(context, id + "F47", { "sketchPlane" : qUnion([Q0])});
            skLineSegment(sketch, "E85.bottom", {"start": v(863.6, 3436.18) * mm, "end": v(0, 3436.18) * mm});
            skLineSegment(sketch, "E85.top", {"start": v(863.6, 2216.98) * mm, "end": v(0, 2216.98) * mm});
            skLineSegment(sketch, "E85.left", {"start": v(863.6, 3436.18) * mm, "end": v(863.6, 2216.98) * mm});
            skLineSegment(sketch, "E85.right", {"start": v(0, 3436.18) * mm, "end": v(0, 2216.98) * mm});
            skSolve(sketch);
        }
        {
            var Q0;
            Q0 = qSketchRegion(id + "F47", true);
            extrude(context, id + "F48", {"entities" : qUnion([Q0]), "depth" : 114.3 * mm});
        }
        {
            var Q0;
            Q0=makeQuery(id+"F48.opExtrude","CAP_FACE",FACE,{"disambiguationData":[OSD([sQuery(id+"F47.wireOp",EDGE,"E85.bottom"),sQuery(id+"F47.wireOp",EDGE,"E85.top"),sQuery(id+"F47.wireOp",EDGE,"E85.left"),sQuery(id+"F47.wireOp",EDGE,"E85.right")])],"isStart":false});
            var sketch = newSketch(context, id + "F49", { "sketchPlane" : qUnion([Q0])});
            skLineSegment(sketch, "E86.0", {"start": v(812.8, 3385.38) * mm, "end": v(812.8, 2267.78) * mm});
            skLineSegment(sketch, "E86.1", {"start": v(812.8, 3385.38) * mm, "end": v(50.8, 3385.38) * mm});
            skLineSegment(sketch, "E86.2", {"start": v(50.8, 3385.38) * mm, "end": v(50.8, 2267.78) * mm});
            skLineSegment(sketch, "E86.3", {"start": v(812.8, 2267.78) * mm, "end": v(50.8, 2267.78) * mm});
            skSolve(sketch);
        }
        {
            var Q0;
            Q0 = qSketchRegion(id + "F49", true);
            extrude(context, id + "F50", {"entities" : qUnion([Q0]), "operationType" : NewBodyOperationType.REMOVE, "oppositeDirection" : true, "depth" : 96.52 * mm, "hasDraft" : true, "draftAngle" : 3 * degree});
        }
        {
            var Q0;
            Q0=makeQuery(id+"F38.opExtrude","SWEPT_FACE",FACE,{"disambiguationData":[OSD([sQuery(id+"F37.wireOp",EDGE,"E66.right")])]});
            var sketch = newSketch(context, id + "F51", { "sketchPlane" : qUnion([Q0])});
            skLineSegment(sketch, "E87.bottom", {"start": v(-4268.1, 38.1) * mm, "end": v(-4318.9, 38.1) * mm});
            skLineSegment(sketch, "E87.top", {"start": v(-4268.1, 152.4) * mm, "end": v(-4318.9, 152.4) * mm});
            skLineSegment(sketch, "E87.left", {"start": v(-4268.1, 38.1) * mm, "end": v(-4268.1, 152.4) * mm});
            skLineSegment(sketch, "E87.right", {"start": v(-4318.9, 38.1) * mm, "end": v(-4318.9, 152.4) * mm});
            skSolve(sketch);
        }
        {
            var Q0;
            Q0 = qSketchRegion(id + "F51", true);
            extrude(context, id + "F52", {"entities" : qUnion([Q0]), "operationType" : NewBodyOperationType.ADD, "depth" : 1235.07 * mm});
        }
    });
